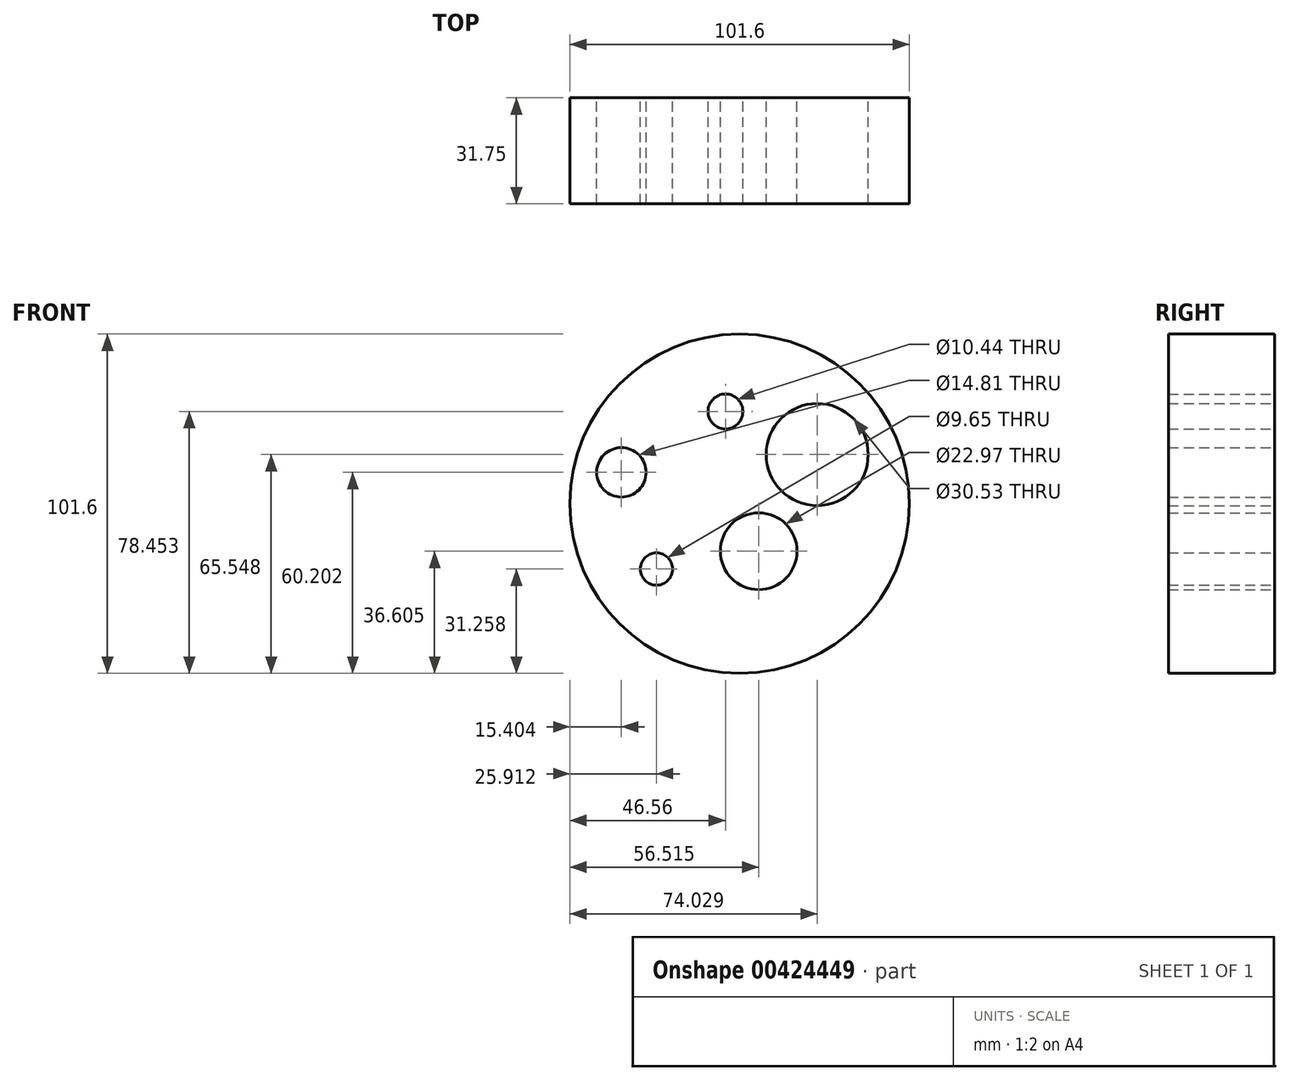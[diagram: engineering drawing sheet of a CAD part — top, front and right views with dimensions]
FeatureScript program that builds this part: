
annotation { "Feature Type Name" : "Feature", "Feature Type Description" : "" }
export const myFeature = defineFeature(function(context is Context, id is Id, definition is map)
    precondition{}
    {
        {
            var Q0;
            Q0=qCreatedBy(makeId("Front.planeOp"),FACE);
            var sketch = newSketch(context, id + "F0", { "sketchPlane" : qUnion([Q0])});
            skCircle(sketch, "E0", {"center": v(0, 0) * mm, "radius": 50.8 * mm});
            skCircle(sketch, "E1", {"center": v(-4.24, 27.65) * mm, "radius": 5.22 * mm});
            skCircle(sketch, "E2", {"center": v(-35.4, 9.4) * mm, "radius": 7.4 * mm});
            skCircle(sketch, "E3", {"center": v(-24.89, -19.54) * mm, "radius": 4.83 * mm});
            skCircle(sketch, "E4", {"center": v(5.72, -14.2) * mm, "radius": 11.48 * mm});
            skCircle(sketch, "E5", {"center": v(23.23, 14.75) * mm, "radius": 15.27 * mm});
            skSolve(sketch);
        }
        {
            var Q0;
            Q0=makeQuery(id+"F0.imprint","IMPRINT",FACE,{"disambiguationData":[TD([[makeQuery(id+"F0.imprint","IMPRINT",EDGE,{"derivedFrom":sQuery(id+"F0.wireOp",EDGE,"E0")}),1.0]])]});
            extrude(context, id + "F1", {"entities" : qUnion([Q0]), "depth" : 31.75 * mm});
        }
    });
